# Revit family: 18 POP
name_source: partatom
category: Furniture
units: mm (PartAtom-declared; Revit-internal decimal feet)

## family parameters
Always vertical = Yes
Cut with Voids When Loaded = No
Room Calculation Point = Yes
Shared = No
Work Plane-Based = Yes

## types (16) — shared parameters
Default Elevation = 1219 mm
Seat_00 = Seat_00
Structure_00 = Structure_00

## per-type parameters (varying)
| type | Armstand_00 | Armstand_01 | Base_00 | Base_01 | Headrest_00 | Seat_01 |
| PP 1_4PPDI02 | Yes | No | Yes | No | Yes | Seat_01 |
| PP 7_4PPDI10 | Yes | No | Yes | No | Yes | Seat_01 |
| PP 1_4PPDI04 | Yes | No | No | Yes | Yes | Seat_01 |
| PP 7_4PPDI12 | Yes | No | No | Yes | Yes | Seat_01 |
| PP 2_4PPGI02 | Yes | No | Yes | No | No | Seat_01 |
| PP 8_4PPGI18 | Yes | No | Yes | No | No | Seat_01 |
| PP 2_4PPGI04 | Yes | No | No | Yes | No | Seat_01 |
| PP 8_4PPGI20 | Yes | No | No | Yes | No | Seat_00 |
| PP 3_4PPGI06 | No | No | Yes | No | No | Seat_01 |
| PP 9_4PPGI22 | No | No | Yes | No | No | Seat_01 |
| PP 3_4PPGI08 | No | No | No | Yes | No | Seat_01 |
| PP 9_4PPGI24 | No | No | No | Yes | No | Seat_01 |
| PP13_4PPGI34 | No | Yes | Yes | No | No | Seat_01 |
| PP15_4PPGI42 | No | Yes | Yes | No | No | Seat_01 |
| PP13_4PPGI36 | No | Yes | No | Yes | No | Seat_01 |
| PP15_4PPGI44 | No | Yes | No | Yes | No | Seat_01 |

## geometry (parser evidence)
native form markers: Sweep x3
no freeform markers — native parametric forms only
